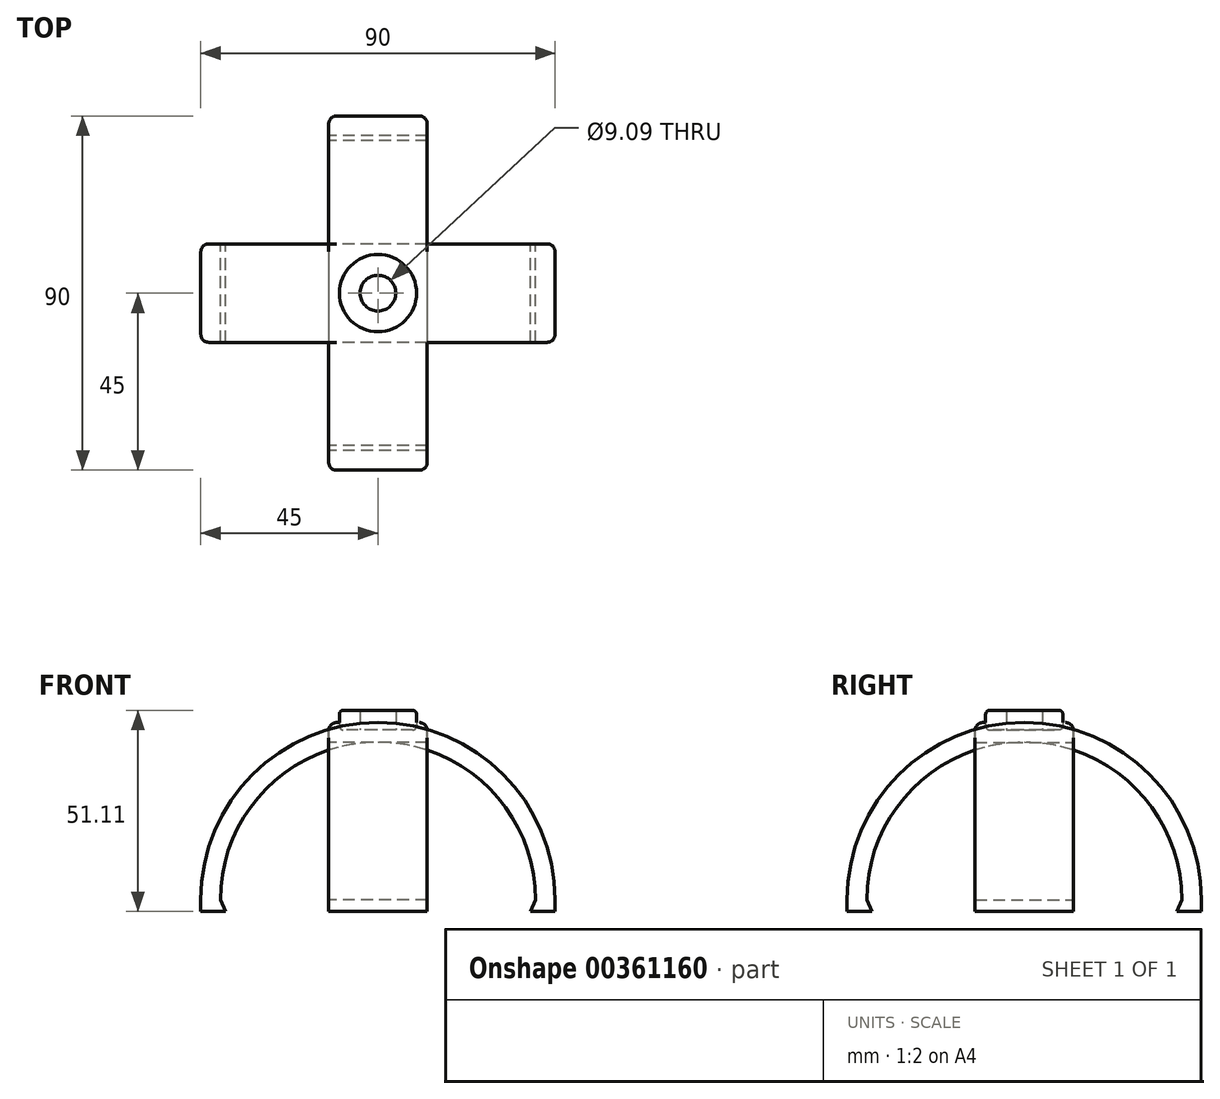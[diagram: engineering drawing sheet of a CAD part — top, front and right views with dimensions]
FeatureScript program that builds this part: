
annotation { "Feature Type Name" : "Feature", "Feature Type Description" : "" }
export const myFeature = defineFeature(function(context is Context, id is Id, definition is map)
    precondition{}
    {
        {
            var Q0;
            Q0=qCreatedBy(makeId("Front.planeOp"),FACE);
            var sketch = newSketch(context, id + "F0", { "sketchPlane" : qUnion([Q0])});
            skArc(sketch, "E0", {"start": v(40, 0) * mm, "mid": v(0, 40) * mm, "end": v(-40, 0) * mm});
            skArc(sketch, "E1", {"start": v(45, 0) * mm, "mid": v(0, 45) * mm, "end": v(-45, 0) * mm});
            skLineSegment(sketch, "E2", {"start": v(40, 0) * mm, "end": v(39, 0) * mm});
            skLineSegment(sketch, "E3", {"start": v(45, 0) * mm, "end": v(45, -3.01) * mm});
            skLineSegment(sketch, "E4", {"start": v(45, -3.01) * mm, "end": v(38.78, -3.01) * mm});
            skLineSegment(sketch, "E5", {"start": v(38.78, -3.01) * mm, "end": v(40, 0) * mm});
            skPoint(sketch, "E6.start.orphan", {"position": v(39.92, -3.01) * mm});
            skLineSegment(sketch, "E7", {"start": v(-45, 0) * mm, "end": v(-45, -2.96) * mm});
            skLineSegment(sketch, "E8", {"start": v(-45, -2.96) * mm, "end": v(-38.7, -2.96) * mm});
            skLineSegment(sketch, "E9", {"start": v(-38.7, -2.96) * mm, "end": v(-40, 0) * mm});
            skPoint(sketch, "E10", {"position": v(0, 45) * mm});
            skSolve(sketch);
        }
        {
            var Q0;
            Q0 = qSketchRegion(id + "F0", true);
            extrude(context, id + "F1", {"entities" : qUnion([Q0]), "depth" : 25 * mm, "symmetric" : true});
        }
        {
            var Q0;
            Q0=qCreatedBy(makeId("Top.planeOp"),FACE);
            cPlane(context, id + "F2", {"entities" : qUnion([Q0]), "cplaneType" : CPlaneType.OFFSET, "offset" : 43.1 * mm, "width" : 150 * mm, "height" : 150 * mm});
        }
        {
            var Q0;
            Q0=qCreatedBy(id+"F2.planeOp",FACE);
            var sketch = newSketch(context, id + "F3", { "sketchPlane" : qUnion([Q0])});
            skCircle(sketch, "E11", {"center": v(0, 0) * mm, "radius": 11 * mm});
            skSolve(sketch);
        }
        {
            var Q0;
            Q0=makeQuery(id+"F1.opExtrude","SWEPT_BODY",BODY,{"disambiguationData":[OSD([sQuery(id+"F0.wireOp",EDGE,"E0"),sQuery(id+"F0.wireOp",EDGE,"E1"),sQuery(id+"F0.wireOp",EDGE,"E3"),sQuery(id+"F0.wireOp",EDGE,"E4"),sQuery(id+"F0.wireOp",EDGE,"E5"),sQuery(id+"F0.wireOp",EDGE,"E7"),sQuery(id+"F0.wireOp",EDGE,"E8"),sQuery(id+"F0.wireOp",EDGE,"E9")])]});
            var Q1;
            Q1=sQuery(id+"F3.wireOp",EDGE,"E11");
            transform(context, id + "F4", {"entities" : qUnion([Q0]), "transformType" : TransformType.ROTATION, "transformAxis" : qUnion([Q1]), "angle" : 90 * degree, "makeCopy" : true});
        }
        {
            var Q0;
            Q0=makeQuery(id+"F4.opPattern","COPY",FACE,{"derivedFrom":makeQuery(id+"F1.opExtrude","SWEPT_FACE",FACE,{"disambiguationData":[OSD([sQuery(id+"F0.wireOp",EDGE,"E1")])]}),"instanceName":"1"});
            var Q1;
            Q1=makeQuery(id+"F1.opExtrude","CAP_EDGE",EDGE,{"disambiguationData":[OSD([sQuery(id+"F0.wireOp",EDGE,"E1")])],"isStart":false});
            var Q2;
            Q2=makeQuery(id+"F1.opExtrude","CAP_EDGE",EDGE,{"disambiguationData":[OSD([sQuery(id+"F0.wireOp",EDGE,"E1")])],"isStart":true});
            var Q3;
            Q3=makeQuery(id+"FmFV28OYi0hSPzb_1.opExtrude","SWEPT_FACE",FACE,{"disambiguationData":[OSD([sQuery(id+"FqsUNTkfbhRvoDG_1.wireOp",EDGE,"Dn9zaHK9-kjnZ-s7Bh-MfFD-7HfGj614pOGq")])]});
            fillet(context, id + "F5", {"entities" : qUnion([Q0, Q1, Q2, Q3]), "radius" : 2 * mm, "tangentPropagation" : true, "allowEdgeOverflow" : false});
        }
        {
            var Q0;
            Q0=qCreatedBy(id+"F2.planeOp",FACE);
            var sketch = newSketch(context, id + "F6", { "sketchPlane" : qUnion([Q0])});
            skCircle(sketch, "E12", {"center": v(0, 0) * mm, "radius": 9.81 * mm});
            skCircle(sketch, "E13", {"center": v(0, 0) * mm, "radius": 4.55 * mm});
            skSolve(sketch);
        }
        {
            var Q0;
            Q0 = qSketchRegion(id + "F6", true);
            extrude(context, id + "F7", {"entities" : qUnion([Q0]), "depth" : 5 * mm});
        }
        {
            var Q0;
            Q0=makeQuery(id+"F7.opExtrude","SWEPT_FACE",FACE,{"disambiguationData":[OSD([sQuery(id+"F6.wireOp",EDGE,"E12")])]});
            fillet(context, id + "F8", {"entities" : qUnion([Q0]), "radius" : 1 * mm, "tangentPropagation" : true, "allowEdgeOverflow" : false});
        }
        {
            var Q0;
            Q0=qCreatedBy(makeId("Front.planeOp"),FACE);
            cPlane(context, id + "F9", {"entities" : qUnion([Q0]), "cplaneType" : CPlaneType.OFFSET, "offset" : 25 * mm, "width" : 150 * mm, "height" : 150 * mm});
        }
    });
